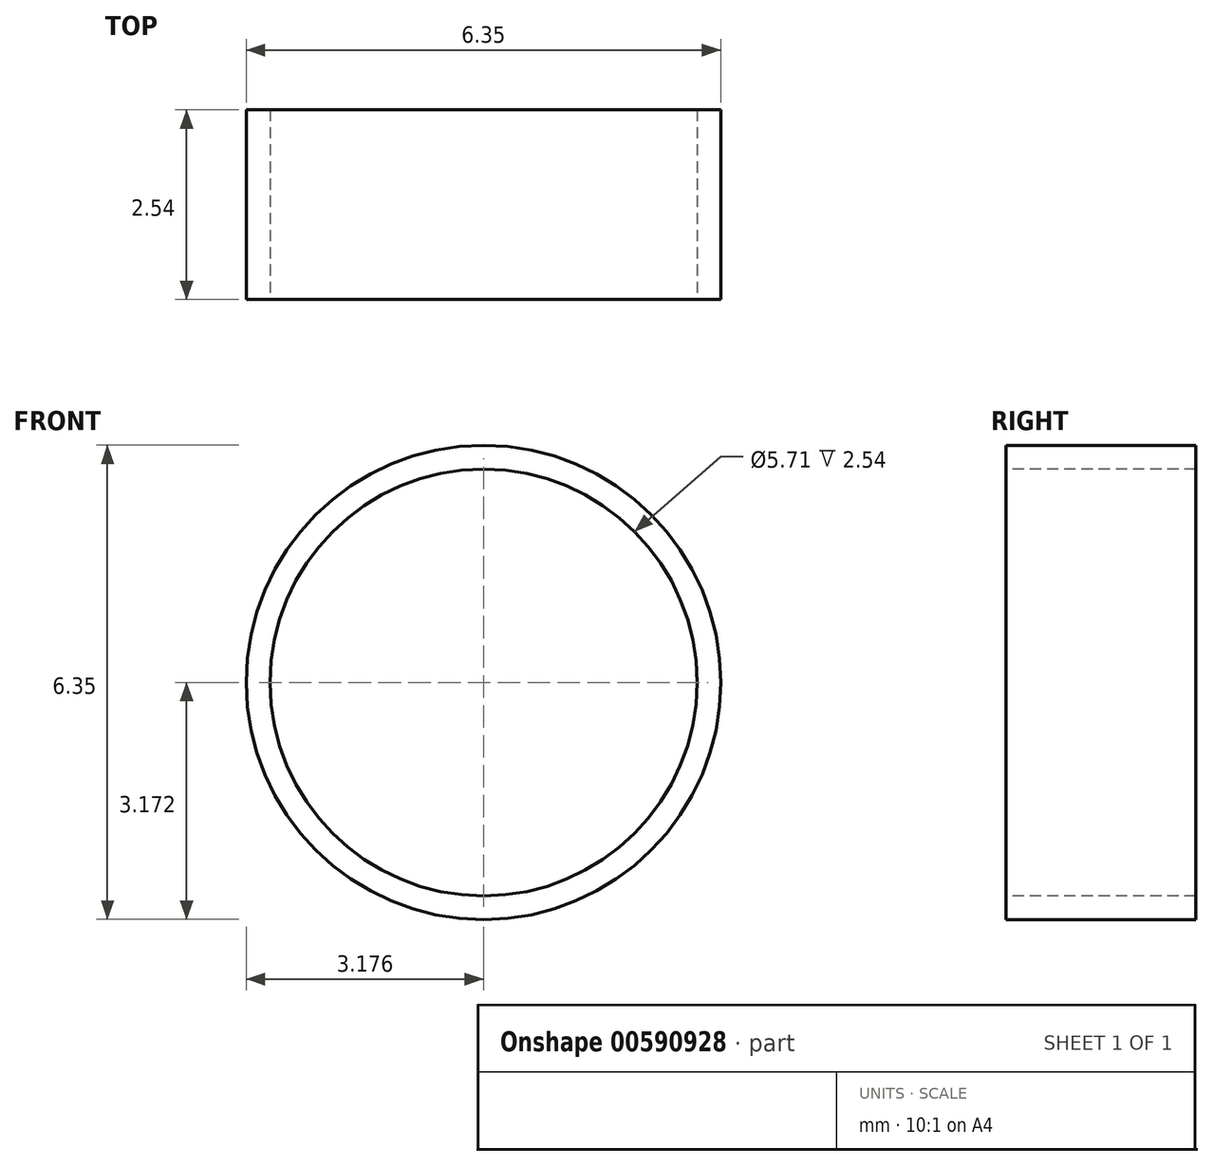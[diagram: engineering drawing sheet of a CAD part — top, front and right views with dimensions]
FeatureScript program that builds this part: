
annotation { "Feature Type Name" : "Feature", "Feature Type Description" : "" }
export const myFeature = defineFeature(function(context is Context, id is Id, definition is map)
    precondition{}
    {
        {
            var Q0;
            Q0=qCreatedBy(makeId("Front.planeOp"),FACE);
            var sketch = newSketch(context, id + "F0", { "sketchPlane" : qUnion([Q0])});
            skCircle(sketch, "E0", {"center": v(-58.06, 49.68) * mm, "radius": 3.18 * mm});
            skSolve(sketch);
        }
        {
            var Q0;
            Q0=makeQuery(id+"F0.imprint","IMPRINT",FACE,{"disambiguationData":[TD([[makeQuery(id+"F0.imprint","IMPRINT",EDGE,{"derivedFrom":sQuery(id+"F0.wireOp",EDGE,"E0")}),1.0]])]});
            extrude(context, id + "F1", {"entities" : qUnion([Q0]), "depth" : 2.54 * mm, "offsetDistance" : 25.4 * mm});
        }
        {
            var Q0;
            Q0=makeQuery(id+"F1.opExtrude","CAP_FACE",FACE,{"disambiguationData":[OSD([sQuery(id+"F0.wireOp",EDGE,"E0")])],"isStart":false});
            var sketch = newSketch(context, id + "F2", { "sketchPlane" : qUnion([Q0])});
            skCircle(sketch, "E1", {"center": v(-58.06, 49.68) * mm, "radius": 2.54 * mm});
            skSolve(sketch);
        }
        {
            var Q0;
            Q0=sQuery(id+"F2.wireOp",VERTEX,"E1.center");
            var Q1;
            Q1=makeQuery(id+"F1.opExtrude","SWEPT_BODY",BODY,{"disambiguationData":[OSD([sQuery(id+"F0.wireOp",EDGE,"E0")])]});
            hole(context, id + "F3", {"style" : HoleStyle.SIMPLE, "endStyle" : HoleEndStyle.THROUGH, "holeDiameter" : 5.7 * mm, "majorDiameter" : 6.35 * mm, "isTappedThrough" : true, "tappedDepth" : 12.7 * mm, "tapClearance" : 3, "locations" : qUnion([Q0]), "scope" : qUnion([Q1])});
        }
    });
